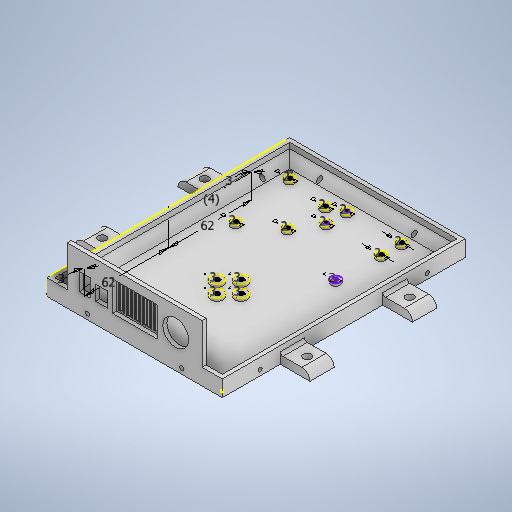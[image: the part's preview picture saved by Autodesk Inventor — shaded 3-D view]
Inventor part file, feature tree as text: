
AUTODESK INVENTOR PART (.ipt)
format: ipt  version: 2025.1 (Build 291241000, 241)  size: 824,832 bytes
history: native  units: mm
features: thread x21, extrude x16, sketch x15, other x4, chamfer x2, fillet x1, imported_body x1
ambient origin geometry x8: Origin, YZ Plane, XZ Plane, XY Plane, X Axis, Y Axis, Z Axis, Center Point
bodies: Body1 (feature_tree)
feature tree (60):
  extrude  "Extrusión6"  Depth=180.0mm
  extrude  "Extrusión7"  Depth=3.0mm
  extrude  "Extrusión13"  Depth=6.0mm
  extrude  "Extrusión12"  Depth=54.0mm
  extrude  "Extrusión11"  Depth=3.0mm
  extrude  "Extrusión8"  Depth=3.0mm
  chamfer  "Chaflán1"  Distance=0.9mm
  extrude  "Extrusión16"  Depth=61.0mm
  extrude  "Extrusión14"  Depth=22.0mm
  extrude  "Extrusión9"  Depth=22.0mm
  extrude  "Extrusión10"  Depth=3.0mm
  extrude  "Extrusión15"  Depth=3.0mm
  extrude  "Extrusión17"  Depth=3.0mm
  extrude  "Extrusión18"  Depth=18.0mm
  chamfer  "Chaflán2"  Distance=102.0mm
  thread  "Rosca13"  [1 undecoded]
  thread  "Rosca14"  [1 undecoded]
  thread  "Rosca15"  [1 undecoded]
  thread  "Rosca16"  [1 undecoded]
  thread  "Rosca17"  [1 undecoded]
  thread  "Rosca18"  [1 undecoded]
  thread  "Rosca19"  [1 undecoded]
  thread  "Rosca20"  [1 undecoded]
  thread  "Rosca21"  [1 undecoded]
  thread  "Rosca22"  [1 undecoded]
  thread  "Rosca23"  [1 undecoded]
  thread  "Rosca24"  [1 undecoded]
  thread  "Rosca25"  [1 undecoded]
  thread  "Rosca26"  [1 undecoded]
  thread  "Rosca27"  [1 undecoded]
  thread  "Rosca28"  [1 undecoded]
  thread  "Rosca29"  [1 undecoded]
  thread  "Rosca30"  [1 undecoded]
  thread  "Rosca31"  [1 undecoded]
  thread  "Rosca32"  [1 undecoded]
  thread  "Rosca33"  [1 undecoded]
  extrude  "Extrusión19"  Depth=2.0mm
  extrude  "Extrusión20"  Depth=2.0mm
  other  "Empalme de cara2"
  other  "Empalme de cara3"
  other  "Empalme de cara4"
  other  "Empalme de cara5"
  fillet  "Empalme2"  Radius=2.0mm
  extrude  "Extrusión24"  Depth=2.0mm
  imported_body  "base"
  sketch  "Boceto10"  dims[d53=130.0mm d54=180.0mm]
  sketch  "Boceto11"  dims[d55=2.0mm d56=0.0mm d57=3.0mm]
  sketch  "Boceto12"  dims[d58=10.0mm d59=0.0mm d60=6.0mm]
  sketch  "Boceto13"  dims[d64=102.0mm d65=54.0mm]
  sketch  "Boceto15"  dims[d71=3.0mm d73=3.0mm]
  sketch  "Boceto16"  dims[d74=14.0mm d75=3.0mm]
  sketch  "Boceto17"  dims[d76=48.0mm]
  sketch  "Boceto18"  dims[d78=82.0mm]
  sketch  "Boceto19"  dims[d80=74.0mm]
  sketch  "Boceto20"  dims[d86=50.8mm]
  sketch  "Boceto21"  dims[d87=15.2mm]
  sketch  "Boceto22"  dims[d88=3.0mm]
  sketch  "Boceto23"  dims[d89=50.8mm]
  sketch  "Boceto24"  dims[d90=4.7mm]
  sketch  "Boceto30"  dims[d91=3.0mm d92=0.9mm d96=61.0mm d97=40.64mm d98=15.24mm d99=3.0mm d100=3.0mm d101=3.0mm d102=18.0mm d103=102.0mm d104=6.0mm d105=3.0mm d106=3.0mm d107=3.0mm d108=3.0mm d109=3.0mm d110=3.0mm d111=3.0mm d112=3.0mm d113=2.0mm d114=2.0mm d115=2.0mm d116=2.0mm d117=2.0mm d118=2.0mm d119=2.0mm d120=2.0mm d121=2.0mm d122=2.0mm d123=0.0mm d124=2.0mm d125=2.0mm d126=2.0mm d127=2.0mm d128=2.0mm d129=2.0mm d130=3.0mm d131=3.0mm d132=3.0mm d133=3.0mm d134=2.0mm d135=2.0mm d136=2.0mm d137=30.0mm d138=0.0mm d139=1.7mm d140=1.7mm d141=1.7mm d142=1.7mm d143=1.7mm d144=1.7mm d145=1.7mm d146=1.7mm d147=1.7mm d148=1.7mm d149=1.7mm d150=1.7mm d151=1.7mm d152=1.0mm d153=0.0mm d155=12.0mm d156=12.0mm d157=12.0mm d158=12.0mm d159=12.0mm d160=12.0mm d161=12.0mm d162=12.0mm d163=3.0mm d164=3.0mm d165=3.0mm d166=3.0mm d167=30.0mm d168=0.0mm d170=7.0mm d171=6.0mm d172=0.0mm d173=7.0mm d174=6.0mm d175=45.0deg d176=15.0mm d177=15.0mm d178=30.0mm d179=0.0mm d182=9.0mm d184=10.0mm d185=0.0mm d186=34.55mm d188=19.1mm d189=60.0mm d190=15.0mm d191=8.0mm d192=13.0mm d193=23.0mm d195=12.0mm d196=20.0mm d198=20.0mm d201=15.0mm d202=24.0mm d203=15.0mm d204=36.0mm d205=1.5mm d207=50.0mm d226=1.5mm d227=2.0mm d228=0.0mm d229=1.0mm d230=2.0mm d231=45.0deg d235=140.0mm d236=0.0mm d237=3.0mm d238=3.0mm d239=3.0mm d240=3.0mm d241=20.0mm d242=0.0mm d243=3.0mm d244=3.0mm d245=12.0mm d246=0.0mm d247=4.0mm d248=4.0mm d249=4.0mm d250=25.0mm d259=3.0mm d260=0.0mm d261=3.0mm d262=0.0mm d263=3.0mm d264=0.0mm d265=3.0mm d266=0.0mm d267=3.0mm d268=0.0mm d269=3.0mm d270=0.0mm d271=3.0mm d272=0.0mm d273=3.0mm d274=0.0mm d275=3.0mm d276=0.0mm d277=2.0mm d278=0.0mm d279=2.0mm d280=0.0mm d281=2.0mm d282=0.0mm d283=2.0mm d284=0.0mm d285=9.417mm d286=0.0mm d287=9.417mm d288=0.0mm d289=9.417mm d290=0.0mm d291=9.417mm d292=0.0mm d293=9.417mm d294=0.0mm d295=9.417mm d296=0.0mm d297=9.417mm d298=0.0mm d299=9.417mm d300=0.0mm d302=38.0mm d304=18.0mm d305=6.0mm d306=9.0mm d307=62.0mm d308=62.0mm d309=22.0mm d310=0.0mm d311=38.0mm d312=9.0mm d313=18.0mm d314=6.0mm d315=22.0mm d316=0.0mm d323=35.0mm d324=35.0mm d327=35.0mm d328=35.0mm d356=2.0mm d357=2.0mm d358=2.0mm d359=2.0mm d360=6.0mm d361=76.0mm d362=76.0mm d363=76.0mm d364=76.0mm d365=6.0mm d366=6.0mm d367=6.0mm d369=6.0mm d370=22.0mm d371=0.0mm]
note: 21 required parameter values undecoded (feature->parameter linkage not recoverable at this tier; creation-order binding heuristic only, values carry confidence <= 0.55)
